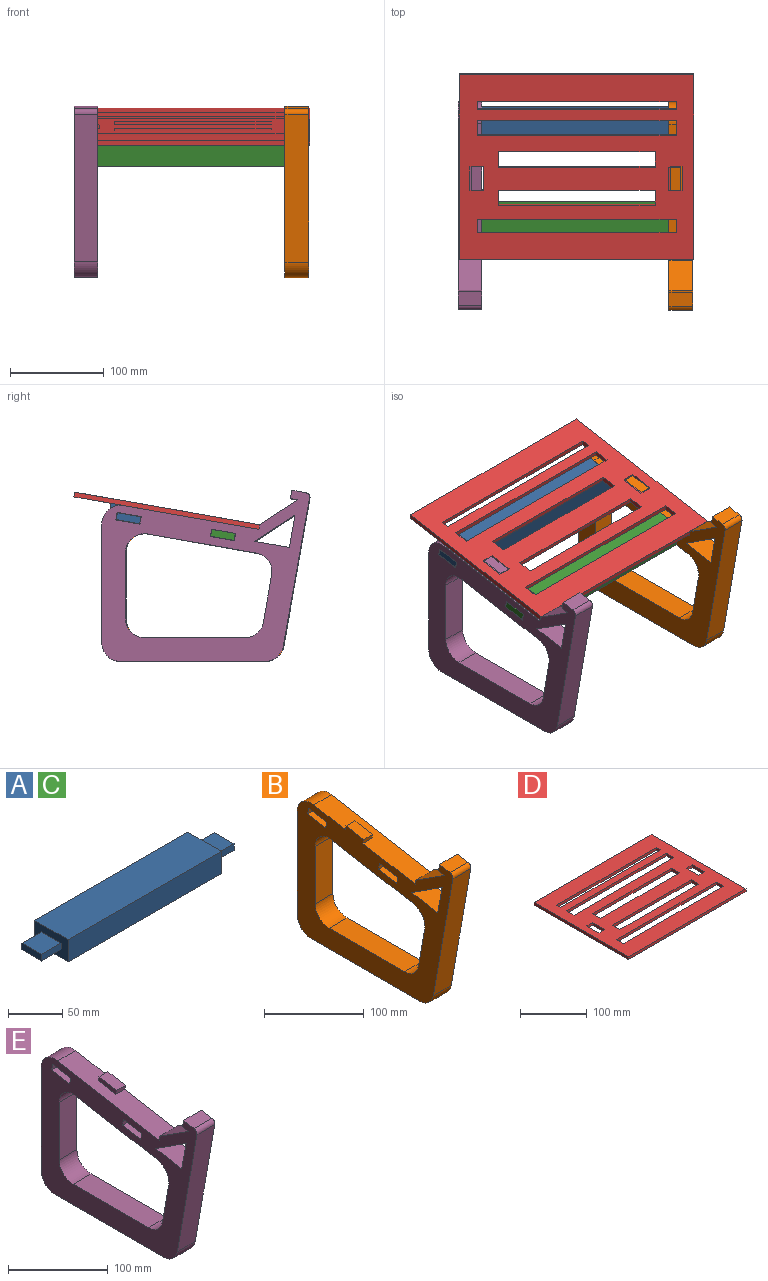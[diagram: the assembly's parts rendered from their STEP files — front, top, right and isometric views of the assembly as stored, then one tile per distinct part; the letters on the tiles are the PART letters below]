
ASSEMBLY  parts=5 mates=6
PART A: 16 faces, bbox 250x43x25 mm
  f0: plane 43x25mm, normal (1,0,0), area 884.5mm2, adj f2,f3,f4,f5,f11,f12,f13,f14
  f1: plane 43x25mm, normal (-1,0,0), area 884.5mm2, adj f2,f3,f4,f5,f6,f7,f8,f9
  f2: plane 199.2x43mm, normal (0,0,-1), area 8565.6mm2, adj f0,f1,f4,f5
  f3: plane 199.2x43mm, normal (0,0,1), area 8565.6mm2, adj f0,f1,f4,f5
  f4: plane 199.2x25mm, normal (0,1,0), area 4980mm2, adj f0,f1,f2,f3
  f5: plane 199.2x25mm, normal (0,-1,0), area 4980mm2, adj f0,f1,f2,f3
  f6: plane 25.4x7.5mm, normal (0,1,0), area 190.5mm2, adj f1,f7,f9,f10
  f7: plane 25.4x25.4mm, normal (0,0,-1), area 645.2mm2, adj f1,f6,f8,f10
  f8: plane 25.4x7.5mm, normal (0,-1,0), area 190.5mm2, adj f1,f7,f9,f10
  f9: plane 25.4x25.4mm, normal (0,0,1), area 645.2mm2, adj f1,f6,f8,f10
  f10: plane 25.4x7.5mm, normal (-1,0,0), area 190.5mm2, adj f6,f7,f8,f9
  f11: plane 25.4x7.5mm, normal (0,-1,0), area 190.5mm2, adj f0,f12,f14,f15
  f12: plane 25.4x25.4mm, normal (0,0,-1), area 645.2mm2, adj f0,f11,f13,f15
  f13: plane 25.4x7.5mm, normal (0,1,0), area 190.5mm2, adj f0,f12,f14,f15
  f14: plane 25.4x25.4mm, normal (0,0,1), area 645.2mm2, adj f0,f11,f13,f15
  f15: plane 25.4x7.5mm, normal (1,0,0), area 190.5mm2, adj f11,f12,f13,f14
PART B: 38 faces, bbox 25.4x221.3x182.4 mm
  f0: plane 12.7x5mm, normal (0,0.98,0.17), area 64.5mm2, adj f1,f31,f35,f37
  f1: plane 25.01x12.7mm, normal (0,-0.17,0.98), area 322.6mm2, adj f0,f20,f35,f37
  f2: plane 25.4x7.88mm, normal (0,0.98,0.17), area 203.2mm2, adj f3,f34,f35,f36
  f3: plane 25.61x25.4mm, normal (0,0.17,-0.98), area 660.4mm2, adj f2,f4,f35,f36
  f4: plane 25.4x7.88mm, normal (0,-0.98,-0.17), area 203.2mm2, adj f3,f34,f35,f36
  f5: plane 25.4x7.88mm, normal (0,0.98,0.17), area 203.2mm2, adj f6,f30,f35,f36
  f6: plane 25.61x25.4mm, normal (0,0.17,-0.98), area 660.4mm2, adj f5,f7,f35,f36
  f7: plane 25.4x7.88mm, normal (0,-0.98,-0.17), area 203.2mm2, adj f6,f30,f35,f36
  f8: plane 25.4x5mm, normal (0,0.98,0.17), area 129mm2, adj f9,f31,f35,f36
  f9: plane 40.61x26.37mm, normal (0,0.54,0.84), area 1229.8mm2, adj f8,f10,f35,f36
  f10: plane 25.4x8.05mm, normal (0,0.17,-0.98), area 207.6mm2, adj f9,f11,f35,f36
  f11: plane 25.4x8.86mm, normal (0,0.98,0.17), area 228.6mm2, adj f10,f12,f35,f36
  f12: plane 25.4x14.77mm, normal (0,-0.17,0.98), area 381mm2, adj f11,f13,f35,f36
  f13: cylinder r=5mm len=25.4mm, axis (1,0,0), area 199.5mm2, adj f12,f14,f35,f36
  f14: plane 157.5x27.77mm, normal (0,-0.98,-0.17), area 4062.2mm2, adj f13,f15,f35,f36
  f15: cylinder r=20mm len=25.4mm, axis (1,0,0), area 709.3mm2, adj f14,f16,f35,f36
  f16: plane 153.72x25.4mm, normal (0,0,-1), area 3904.4mm2, adj f15,f17,f35,f36
  f17: cylinder r=20mm len=25.4mm, axis (1,0,0), area 798mm2, adj f16,f18,f35,f36
  f18: plane 126.44x25.4mm, normal (0,1,0), area 3211.7mm2, adj f17,f19,f35,f36
  f19: cylinder r=20mm len=25.4mm, axis (1,0,0), area 886.6mm2, adj f18,f31,f35,f36
  f20: plane 12.7x5mm, normal (0,-0.98,-0.17), area 64.5mm2, adj f1,f31,f35,f37
  f21: cylinder r=20mm len=25.4mm, axis (1,0,0), area 798mm2, adj f22,f32,f35,f36
  f22: plane 115.88x25.4mm, normal (0,0.17,-0.98), area 2988.8mm2, adj f21,f23,f35,f36
  f23: cylinder r=20mm len=25.4mm, axis (1,0,0), area 886.6mm2, adj f22,f24,f35,f36
  f24: plane 70.77x25.4mm, normal (0,-1,0), area 1797.6mm2, adj f23,f25,f35,f36
  f25: cylinder r=20mm len=25.4mm, axis (1,0,0), area 798mm2, adj f24,f26,f35,f36
  f26: plane 107.01x25.4mm, normal (0,0,1), area 2717.9mm2, adj f25,f27,f35,f36
  f27: cylinder r=20mm len=25.4mm, axis (1,0,0), area 709.3mm2, adj f26,f32,f35,f36
  f28: plane 34.4x25.4mm, normal (0,0.98,0.17), area 887.2mm2, adj f29,f33,f35,f36
  f29: plane 42.95x27.89mm, normal (0,-0.54,-0.84), area 1300.9mm2, adj f28,f33,f35,f36
  f30: plane 25.61x25.4mm, normal (0,-0.17,0.98), area 660.4mm2, adj f5,f7,f35,f36
  f31: plane 143.88x25.4mm, normal (0,-0.17,0.98), area 3388.5mm2, adj f0,f8,f19,f20,f35,f36,f37
  f32: plane 50.34x25.4mm, normal (0,0.98,0.17), area 1298.4mm2, adj f21,f27,f35,f36
  f33: plane 36.89x25.4mm, normal (0,-0.17,0.98), area 951.4mm2, adj f28,f29,f35,f36
  f34: plane 25.61x25.4mm, normal (0,-0.17,0.98), area 660.4mm2, adj f2,f4,f35,f36
  f35: plane 221.26x182.42mm, normal (-1,0,0), area 16033mm2, adj f0,f1,f2,f3,f4,f5,f6,f7
  f36: plane 221.26x182.42mm, normal (1,0,0), area 15903.9mm2, adj f2,f3,f4,f5,f6,f7,f8,f9
  f37: plane 25.9x9.41mm, normal (1,0,0), area 129mm2, adj f0,f1,f20,f31
PART C: same geometry as A
PART D: 34 faces, bbox 250x200x5.1 mm
  f0: plane 12.7x5.08mm, normal (0,1,0), area 64.5mm2, adj f1,f31,f32,f33
  f1: plane 26x5.08mm, normal (1,0,0), area 132.1mm2, adj f0,f2,f32,f33
  f2: plane 12.7x5.08mm, normal (0,-1,0), area 64.5mm2, adj f1,f31,f32,f33
  f3: plane 26x5.08mm, normal (1,0,0), area 132.1mm2, adj f4,f24,f32,f33
  f4: plane 12.7x5.08mm, normal (0,-1,0), area 64.5mm2, adj f3,f5,f32,f33
  f5: plane 26x5.08mm, normal (-1,0,0), area 132.1mm2, adj f4,f24,f32,f33
  f6: plane 200x5.08mm, normal (1,0,0), area 1016mm2, adj f7,f25,f32,f33
  f7: plane 250x5.08mm, normal (0,1,0), area 1270mm2, adj f6,f8,f32,f33
  f8: plane 200x5.08mm, normal (-1,0,0), area 1016mm2, adj f7,f25,f32,f33
  f9: plane 15x5.08mm, normal (1,0,0), area 76.2mm2, adj f10,f26,f32,f33
  f10: plane 211.9x5.08mm, normal (0,-1,0), area 1076.5mm2, adj f9,f11,f32,f33
  f11: plane 15x5.08mm, normal (-1,0,0), area 76.2mm2, adj f10,f26,f32,f33
  f12: plane 211.9x5.08mm, normal (0,1,0), area 1076.5mm2, adj f13,f27,f32,f33
  f13: plane 8.66x5.08mm, normal (1,0,0), area 44mm2, adj f12,f14,f32,f33
  f14: plane 211.9x5.08mm, normal (0,-1,0), area 1076.5mm2, adj f13,f27,f32,f33
  f15: plane 211.9x5.08mm, normal (0,1,0), area 1076.5mm2, adj f16,f28,f32,f33
  f16: plane 16.26x5.08mm, normal (1,0,0), area 82.6mm2, adj f15,f17,f32,f33
  f17: plane 211.9x5.08mm, normal (0,-1,0), area 1076.5mm2, adj f16,f28,f32,f33
  f18: plane 17x5.08mm, normal (1,0,0), area 86.4mm2, adj f19,f29,f32,f33
  f19: plane 167.2x5.08mm, normal (0,-1,0), area 849.4mm2, adj f18,f20,f32,f33
  f20: plane 17x5.08mm, normal (-1,0,0), area 86.4mm2, adj f19,f29,f32,f33
  f21: plane 16x5.08mm, normal (1,0,0), area 81.3mm2, adj f22,f30,f32,f33
  f22: plane 167.2x5.08mm, normal (0,-1,0), area 849.4mm2, adj f21,f23,f32,f33
  f23: plane 16x5.08mm, normal (-1,0,0), area 81.3mm2, adj f22,f30,f32,f33
  f24: plane 12.7x5.08mm, normal (0,1,0), area 64.5mm2, adj f3,f5,f32,f33
  f25: plane 250x5.08mm, normal (0,-1,0), area 1270mm2, adj f6,f8,f32,f33
  f26: plane 211.9x5.08mm, normal (0,1,0), area 1076.5mm2, adj f9,f11,f32,f33
  f27: plane 8.66x5.08mm, normal (-1,0,0), area 44mm2, adj f12,f14,f32,f33
  f28: plane 16.26x5.08mm, normal (-1,0,0), area 82.6mm2, adj f15,f17,f32,f33
  f29: plane 167.2x5.08mm, normal (0,1,0), area 849.4mm2, adj f18,f20,f32,f33
  f30: plane 167.2x5.08mm, normal (0,1,0), area 849.4mm2, adj f21,f23,f32,f33
  f31: plane 26x5.08mm, normal (-1,0,0), area 132.1mm2, adj f0,f2,f32,f33
  f32: plane 250x200mm, normal (0,0,1), area 35363.2mm2, adj f0,f1,f2,f3,f4,f5,f6,f7
  f33: plane 250x200mm, normal (0,0,-1), area 35363.2mm2, adj f0,f1,f2,f3,f4,f5,f6,f7
PART E: 38 faces, bbox 25.4x221.3x182.4 mm
  f0: plane 12.7x5mm, normal (0,0.98,0.17), area 64.5mm2, adj f1,f31,f35,f37
  f1: plane 25.01x12.7mm, normal (0,-0.17,0.98), area 322.6mm2, adj f0,f20,f35,f37
  f2: plane 25.4x7.88mm, normal (0,0.98,0.17), area 203.2mm2, adj f3,f34,f35,f36
  f3: plane 25.61x25.4mm, normal (0,0.17,-0.98), area 660.4mm2, adj f2,f4,f35,f36
  f4: plane 25.4x7.88mm, normal (0,-0.98,-0.17), area 203.2mm2, adj f3,f34,f35,f36
  f5: plane 25.4x7.88mm, normal (0,0.98,0.17), area 203.2mm2, adj f6,f30,f35,f36
  f6: plane 25.61x25.4mm, normal (0,0.17,-0.98), area 660.4mm2, adj f5,f7,f35,f36
  f7: plane 25.4x7.88mm, normal (0,-0.98,-0.17), area 203.2mm2, adj f6,f30,f35,f36
  f8: plane 25.4x5mm, normal (0,0.98,0.17), area 129mm2, adj f9,f31,f35,f36
  f9: plane 40.61x26.37mm, normal (0,0.54,0.84), area 1229.8mm2, adj f8,f10,f35,f36
  f10: plane 25.4x8.05mm, normal (0,0.17,-0.98), area 207.6mm2, adj f9,f11,f35,f36
  f11: plane 25.4x8.86mm, normal (0,0.98,0.17), area 228.6mm2, adj f10,f12,f35,f36
  f12: plane 25.4x14.77mm, normal (0,-0.17,0.98), area 381mm2, adj f11,f13,f35,f36
  f13: cylinder r=5mm len=25.4mm, axis (-1,0,0), area 199.5mm2, adj f12,f14,f35,f36
  f14: plane 157.5x27.77mm, normal (0,-0.98,-0.17), area 4062.2mm2, adj f13,f15,f35,f36
  f15: cylinder r=20mm len=25.4mm, axis (-1,0,0), area 709.3mm2, adj f14,f16,f35,f36
  f16: plane 153.72x25.4mm, normal (0,0,-1), area 3904.4mm2, adj f15,f17,f35,f36
  f17: cylinder r=20mm len=25.4mm, axis (-1,0,0), area 798mm2, adj f16,f18,f35,f36
  f18: plane 126.44x25.4mm, normal (0,1,0), area 3211.7mm2, adj f17,f19,f35,f36
  f19: cylinder r=20mm len=25.4mm, axis (-1,0,0), area 886.6mm2, adj f18,f31,f35,f36
  f20: plane 12.7x5mm, normal (0,-0.98,-0.17), area 64.5mm2, adj f1,f31,f35,f37
  f21: cylinder r=20mm len=25.4mm, axis (-1,0,0), area 798mm2, adj f22,f32,f35,f36
  f22: plane 115.88x25.4mm, normal (0,0.17,-0.98), area 2988.8mm2, adj f21,f23,f35,f36
  f23: cylinder r=20mm len=25.4mm, axis (-1,0,0), area 886.6mm2, adj f22,f24,f35,f36
  f24: plane 70.77x25.4mm, normal (0,-1,0), area 1797.6mm2, adj f23,f25,f35,f36
  f25: cylinder r=20mm len=25.4mm, axis (-1,0,0), area 798mm2, adj f24,f26,f35,f36
  f26: plane 107.01x25.4mm, normal (0,0,1), area 2717.9mm2, adj f25,f27,f35,f36
  f27: cylinder r=20mm len=25.4mm, axis (-1,0,0), area 709.3mm2, adj f26,f32,f35,f36
  f28: plane 34.4x25.4mm, normal (0,0.98,0.17), area 887.2mm2, adj f29,f33,f35,f36
  f29: plane 42.95x27.89mm, normal (0,-0.54,-0.84), area 1300.9mm2, adj f28,f33,f35,f36
  f30: plane 25.61x25.4mm, normal (0,-0.17,0.98), area 660.4mm2, adj f5,f7,f35,f36
  f31: plane 143.88x25.4mm, normal (0,-0.17,0.98), area 3388.5mm2, adj f0,f8,f19,f20,f35,f36,f37
  f32: plane 50.34x25.4mm, normal (0,0.98,0.17), area 1298.4mm2, adj f21,f27,f35,f36
  f33: plane 36.89x25.4mm, normal (0,-0.17,0.98), area 951.4mm2, adj f28,f29,f35,f36
  f34: plane 25.61x25.4mm, normal (0,-0.17,0.98), area 660.4mm2, adj f2,f4,f35,f36
  f35: plane 221.26x182.42mm, normal (1,0,0), area 16033mm2, adj f0,f1,f2,f3,f4,f5,f6,f7
  f36: plane 221.26x182.42mm, normal (-1,0,0), area 15903.9mm2, adj f2,f3,f4,f5,f6,f7,f8,f9
  f37: plane 25.9x9.41mm, normal (-1,0,0), area 129mm2, adj f0,f1,f20,f31
PLACE A rot(axis=(1,0,0),10deg) t=(-75.18,36.94,40.83)mm
PLACE B t=(-458.18,-20.24,-59.86)mm
PLACE C rot(axis=(1,0,0),10deg) t=(-75.18,-63.71,23.08)mm
PLACE D rot(axis=(1,0,0),10deg) t=(-73.87,15.84,62.57)mm
PLACE E t=(-200.18,-19.67,-59.59)mm
MATE slider C.f14 <-> B.f3  axis (0,-0.17,0.98) through (37.12,-45.7,43.01)mm
MATE planar A.f3 <-> B.f31  axis (0,-0.17,0.98) through (-75.18,53.77,69.18)mm
MATE slider C.f9 <-> E.f3  axis (0,-0.17,0.98) through (-187.48,-45.1,43.11)mm
MATE planar C.f3 <-> B.f31  axis (0,-0.17,0.98) through (-75.18,-46.88,51.43)mm
MATE planar D.f25 <-> E.f8  axis (0,-0.98,-0.17) through (-73.87,-83.08,47.7)mm
MATE slider A.f9 <-> E.f6  axis (0,-0.17,0.98) through (-187.48,55.54,60.86)mm
